# Revit family: Shower-Outlet-Dorf Bliss-System1
name_source: partatom
category: Plumbing Fixtures
revit_build: Autodesk Revit 2013 (Build: 20121003_2115(x64)
units: mm (PartAtom-declared; Revit-internal decimal feet)

## types (1)
- Standard
    Assembly Code = D2010710
    CW Connection = Yes
    Connector Radius = 10 mm  [stored 0.0328084 ft]
    Cost = 953.64 $
    Default Elevation = 1750 mm  [stored 5.74147 ft]
    Description = Caroma Bliss Shower System
    HW Connection = Yes
    HWFU = 2.37
    Manufacturer = GWA Bathrooms & Kitchens
    Material_ANZRS = Metal-Chrome-Caroma
    Model = 1886.043A
    ModifiedIssue_ANZRS = 2013.2 $
    Type Comments = WELS 3 star rated, 9L/min
    URL = http://dorf.com.au
    Vent Connection = No
    Waste Connection = No

note: [stored X ft] marks values corroborated as IEEE doubles in the binary element streams (Revit-internal decimal feet)

## geometry (parser evidence)
native form markers: Sweep x3
no freeform markers — native parametric forms only
